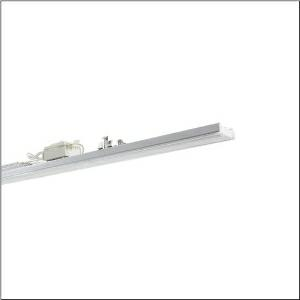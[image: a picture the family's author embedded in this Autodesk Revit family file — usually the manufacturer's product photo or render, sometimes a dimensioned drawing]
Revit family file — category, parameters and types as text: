
# Revit family: licross_r__11_recessed_mo_51tl12dn455gd_2dc2
name_source: partatom
category: Lighting Fixtures
units: mm (PartAtom-declared; Revit-internal decimal feet)

## family parameters
Cut with Voids When Loaded = No
Host = Face
Light Source = No
Part Type = Normal
Room Calculation Point = No
Round Connector Dimension = Use Diameter
Shared = No

## types (1)
- --- (1 x LED, 860 lm, 5.3 W, 4000K)
    Apparent Load = 5 VA
    CIE Flux Codes = 67 92 99 100 100
    Color Rendering = 80
    Color Temperature = 4000K
    Default Elevation = 1800 mm
    Description = Licross® 11 Recessed MO, luminaire insert, of sheet steel, coil coated, white, length: 1.500mm, width: 66mm, height: 67mm, LED rated luminous flux: 5.700lm, light colour: 840, control gear: DALI 2 (for two DALI lines), with plug, 6-pole, with phase selection, mains connection: 220..240V, AC/DC, 0/50..60Hz, rated input power: 30W, without changeover relay, for emergency light function, for central battery installations according to DIN EN 60598-2-22, halogen-free wiring, primary optical cover: cover, of PMMA, light emission: direct distribution, primary light characteristic: symmetric, protection rating (complete): IP40, insulation class (complete): insulation class I (protective earthing), certification: CE, ENEC, VDE, UKCA, protection symbol: D if used in an environment without relevant dust loads with corresponding accessories, impact resistance: IK06, permissible ambient temperature for indoor applications: -25..+45°C, standard: EN 60598-2-22, corresponds to IFS (International Featured Standards) requirements for safety and quality in the food industry, reducing of maximum allowable ambient temperature of 5°C with ceiling mounting, LABS conformity tested according to VDMA 24364:2018-05, packaging unit: 1 piece
    Height = 58 mm
    Lamp = 1 x LED
    Lamp Light Flux = 860 lm
    Lamp Power = 5.3 W
    Lamp count = 1
    Length = 1500 mm
    Luminous efficacy = 162 lm/W
    Manufacturer = Siteco
    ModVariant = No
    Model = 51TL12DN455GD
    Mounting Place = Ceiling
    Mounting Type = Pendant
    Number of Poles = 1
    OnlyDefault = Yes
    Power Factor = 1
    Product Name = Licross® 11 Recessed MO
    Product group = luminaire insert
    ProductGroupID = 902
    Protection Class = Protection class I
    Protection Degree = IP 40
    RLX_Detail_Level = 1
    RLX_Emergency_Light_Flux = 0 lm
    RLX_Emergency_Type = 0
    RLX_Emergency_Type_DB = No
    RlxData = <blob elided: 24493 chars, md5=91d35e16>
    Socket = socket
    Standby Power = 0 W
    System Light Flux = 860 lm
    System Power = 5 W
    Type Comments = : DC mode (central or group accumulator) initial emergency light level
    Type Image = l_1296930.jpg
    URL = http://relux.com
    VarID = @adj_087470
    Voltage = 0 V
    Weight = 0.00 kg
    Width = 66 mm

## geometry (parser evidence)
native form markers: Blend x4, Sweep x9
no freeform markers — native parametric forms only
